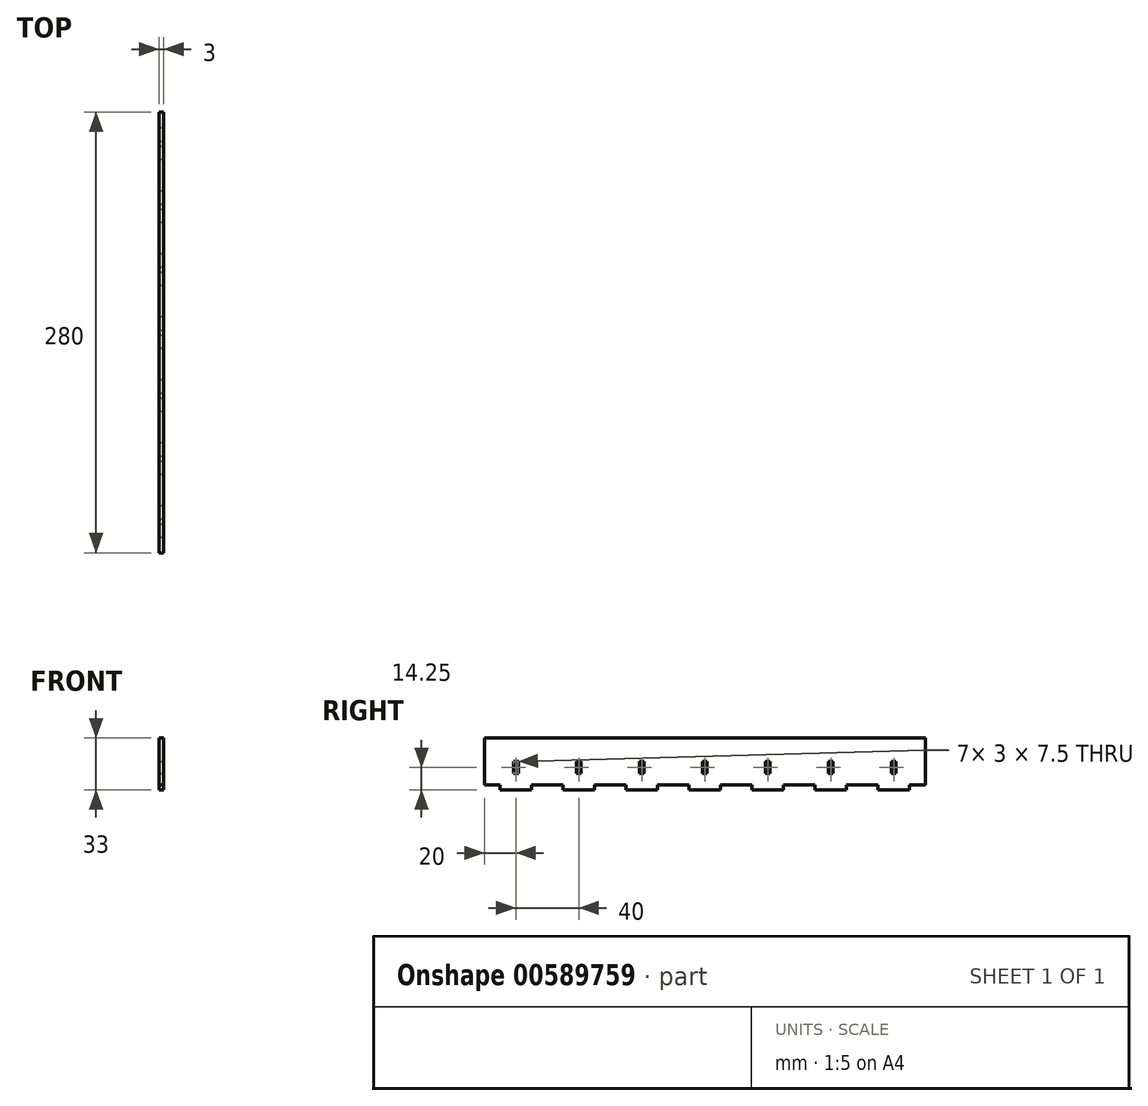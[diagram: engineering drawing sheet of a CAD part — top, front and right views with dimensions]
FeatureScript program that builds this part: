
annotation { "Feature Type Name" : "Feature", "Feature Type Description" : "" }
export const myFeature = defineFeature(function(context is Context, id is Id, definition is map)
    precondition{}
    {
        {
            var Q0;
            Q0=qCreatedBy(makeId("Right.planeOp"),FACE);
            var sketch = newSketch(context, id + "F0", { "sketchPlane" : qUnion([Q0])});
            skLineSegment(sketch, "E0.bottom", {"start": v(140, -15) * mm, "end": v(-140, -15) * mm});
            skLineSegment(sketch, "E0.top", {"start": v(140, 15) * mm, "end": v(-140, 15) * mm});
            skLineSegment(sketch, "E0.left", {"start": v(140, -15) * mm, "end": v(140, 15) * mm});
            skLineSegment(sketch, "E0.right", {"start": v(-140, -15) * mm, "end": v(-140, 15) * mm});
            skPoint(sketch, "E0.middle", {"position": v(0, 0) * mm});
            skSolve(sketch);
        }
        {
            var Q0;
            Q0 = qSketchRegion(id + "F0", true);
            extrude(context, id + "F1", {"entities" : qUnion([Q0]), "depth" : 3 * mm, "offsetDistance" : 25 * mm});
        }
        {
            var Q0;
            Q0=makeQuery(id+"F1.opExtrude","CAP_FACE",FACE,{"disambiguationData":[OSD([sQuery(id+"F0.wireOp",EDGE,"E0.bottom"),sQuery(id+"F0.wireOp",EDGE,"E0.top"),sQuery(id+"F0.wireOp",EDGE,"E0.left"),sQuery(id+"F0.wireOp",EDGE,"E0.right")])],"isStart":false});
            var sketch = newSketch(context, id + "F2", { "sketchPlane" : qUnion([Q0])});
            skLineSegment(sketch, "E1", {"start": v(140, -15) * mm, "end": v(130, -15) * mm, "construction": true});
            skLineSegment(sketch, "E2.bottom", {"start": v(130, -15) * mm, "end": v(110, -15) * mm});
            skLineSegment(sketch, "E2.top", {"start": v(130, -18) * mm, "end": v(110, -18) * mm});
            skLineSegment(sketch, "E2.left", {"start": v(130, -15) * mm, "end": v(130, -18) * mm});
            skLineSegment(sketch, "E2.right", {"start": v(110, -15) * mm, "end": v(110, -18) * mm});
            skLineSegment(sketch, "E3.1.0.0", {"start": v(90, -15) * mm, "end": v(90, -18) * mm});
            skLineSegment(sketch, "E3.1.0.1", {"start": v(90, -15) * mm, "end": v(70, -15) * mm});
            skLineSegment(sketch, "E3.1.0.2", {"start": v(90, -18) * mm, "end": v(70, -18) * mm});
            skLineSegment(sketch, "E3.1.0.3", {"start": v(70, -15) * mm, "end": v(70, -18) * mm});
            skLineSegment(sketch, "E3.2.0.0", {"start": v(50, -15) * mm, "end": v(50, -18) * mm});
            skLineSegment(sketch, "E3.2.0.1", {"start": v(50, -15) * mm, "end": v(30, -15) * mm});
            skLineSegment(sketch, "E3.2.0.2", {"start": v(50, -18) * mm, "end": v(30, -18) * mm});
            skLineSegment(sketch, "E3.2.0.3", {"start": v(30, -15) * mm, "end": v(30, -18) * mm});
            skLineSegment(sketch, "E3.3.0.0", {"start": v(10, -15) * mm, "end": v(10, -18) * mm});
            skLineSegment(sketch, "E3.3.0.1", {"start": v(10, -15) * mm, "end": v(-10, -15) * mm});
            skLineSegment(sketch, "E3.3.0.2", {"start": v(10, -18) * mm, "end": v(-10, -18) * mm});
            skLineSegment(sketch, "E3.3.0.3", {"start": v(-10, -15) * mm, "end": v(-10, -18) * mm});
            skLineSegment(sketch, "E3.4.0.0", {"start": v(-30, -15) * mm, "end": v(-30, -18) * mm});
            skLineSegment(sketch, "E3.4.0.1", {"start": v(-30, -15) * mm, "end": v(-50, -15) * mm});
            skLineSegment(sketch, "E3.4.0.2", {"start": v(-30, -18) * mm, "end": v(-50, -18) * mm});
            skLineSegment(sketch, "E3.4.0.3", {"start": v(-50, -15) * mm, "end": v(-50, -18) * mm});
            skLineSegment(sketch, "E3.5.0.0", {"start": v(-70, -15) * mm, "end": v(-70, -18) * mm});
            skLineSegment(sketch, "E3.5.0.1", {"start": v(-70, -15) * mm, "end": v(-90, -15) * mm});
            skLineSegment(sketch, "E3.5.0.2", {"start": v(-70, -18) * mm, "end": v(-90, -18) * mm});
            skLineSegment(sketch, "E3.5.0.3", {"start": v(-90, -15) * mm, "end": v(-90, -18) * mm});
            skLineSegment(sketch, "E3.6.0.0", {"start": v(-110, -15) * mm, "end": v(-110, -18) * mm});
            skLineSegment(sketch, "E3.6.0.1", {"start": v(-110, -15) * mm, "end": v(-130, -15) * mm});
            skLineSegment(sketch, "E3.6.0.2", {"start": v(-110, -18) * mm, "end": v(-130, -18) * mm});
            skLineSegment(sketch, "E3.6.0.3", {"start": v(-130, -15) * mm, "end": v(-130, -18) * mm});
            skLineSegment(sketch, "E3.direction1", {"start": v(130, -18) * mm, "end": v(90, -18) * mm, "construction": true});
            skSolve(sketch);
        }
        {
            var Q0;
            Q0 = qSketchRegion(id + "F2", true);
            var Q1;
            Q1=makeQuery(id+"F1.opExtrude","CAP_FACE",FACE,{"disambiguationData":[OSD([sQuery(id+"F0.wireOp",EDGE,"E0.bottom"),sQuery(id+"F0.wireOp",EDGE,"E0.top"),sQuery(id+"F0.wireOp",EDGE,"E0.left"),sQuery(id+"F0.wireOp",EDGE,"E0.right")])],"isStart":true});
            extrude(context, id + "F3", {"entities" : qUnion([Q0]), "operationType" : NewBodyOperationType.ADD, "endBound" : BoundingType.UP_TO_SURFACE, "oppositeDirection" : true, "depth" : 25 * mm, "endBoundEntityFace" : qUnion([Q1]), "offsetDistance" : 25 * mm});
        }
        {
            var Q0;
            Q0=makeQuery(id+"F3.boolean.opBoolean","MERGE",FACE,{"derivedFrom":[makeQuery(id+"F1.opExtrude","CAP_FACE",FACE,{"disambiguationData":[OSD([sQuery(id+"F0.wireOp",EDGE,"E0.bottom"),sQuery(id+"F0.wireOp",EDGE,"E0.top"),sQuery(id+"F0.wireOp",EDGE,"E0.left"),sQuery(id+"F0.wireOp",EDGE,"E0.right")])],"isStart":false}),makeQuery(id+"F3.opExtrude","CAP_FACE",FACE,{"disambiguationData":[OSD([sQuery(id+"F2.wireOp",EDGE,"E2.bottom"),sQuery(id+"F2.wireOp",EDGE,"E2.top"),sQuery(id+"F2.wireOp",EDGE,"E2.left"),sQuery(id+"F2.wireOp",EDGE,"E2.right")])],"isStart":true}),makeQuery(id+"F3.opExtrude","CAP_FACE",FACE,{"disambiguationData":[OSD([sQuery(id+"F2.wireOp",EDGE,"E3.1.0.0"),sQuery(id+"F2.wireOp",EDGE,"E3.1.0.1"),sQuery(id+"F2.wireOp",EDGE,"E3.1.0.2"),sQuery(id+"F2.wireOp",EDGE,"E3.1.0.3")])],"isStart":true}),makeQuery(id+"F3.opExtrude","CAP_FACE",FACE,{"disambiguationData":[OSD([sQuery(id+"F2.wireOp",EDGE,"E3.2.0.0"),sQuery(id+"F2.wireOp",EDGE,"E3.2.0.1"),sQuery(id+"F2.wireOp",EDGE,"E3.2.0.2"),sQuery(id+"F2.wireOp",EDGE,"E3.2.0.3")])],"isStart":true}),makeQuery(id+"F3.opExtrude","CAP_FACE",FACE,{"disambiguationData":[OSD([sQuery(id+"F2.wireOp",EDGE,"E3.3.0.0"),sQuery(id+"F2.wireOp",EDGE,"E3.3.0.1"),sQuery(id+"F2.wireOp",EDGE,"E3.3.0.2"),sQuery(id+"F2.wireOp",EDGE,"E3.3.0.3")])],"isStart":true}),makeQuery(id+"F3.opExtrude","CAP_FACE",FACE,{"disambiguationData":[OSD([sQuery(id+"F2.wireOp",EDGE,"E3.4.0.0"),sQuery(id+"F2.wireOp",EDGE,"E3.4.0.1"),sQuery(id+"F2.wireOp",EDGE,"E3.4.0.2"),sQuery(id+"F2.wireOp",EDGE,"E3.4.0.3")])],"isStart":true}),makeQuery(id+"F3.opExtrude","CAP_FACE",FACE,{"disambiguationData":[OSD([sQuery(id+"F2.wireOp",EDGE,"E3.5.0.0"),sQuery(id+"F2.wireOp",EDGE,"E3.5.0.1"),sQuery(id+"F2.wireOp",EDGE,"E3.5.0.2"),sQuery(id+"F2.wireOp",EDGE,"E3.5.0.3")])],"isStart":true}),makeQuery(id+"F3.opExtrude","CAP_FACE",FACE,{"disambiguationData":[OSD([sQuery(id+"F2.wireOp",EDGE,"E3.6.0.0"),sQuery(id+"F2.wireOp",EDGE,"E3.6.0.1"),sQuery(id+"F2.wireOp",EDGE,"E3.6.0.2"),sQuery(id+"F2.wireOp",EDGE,"E3.6.0.3")])],"isStart":true})]});
            var sketch = newSketch(context, id + "F4", { "sketchPlane" : qUnion([Q0])});
            skLineSegment(sketch, "E4", {"start": v(130, -15) * mm, "end": v(110, -15) * mm, "construction": true});
            skLineSegment(sketch, "E5", {"start": v(120, -15) * mm, "end": v(120, -3.75) * mm, "construction": true});
            skLineSegment(sketch, "E6.bottom", {"start": v(121.5, -7.5) * mm, "end": v(118.5, -7.5) * mm});
            skLineSegment(sketch, "E6.top", {"start": v(121.5, 0) * mm, "end": v(118.5, 0) * mm});
            skLineSegment(sketch, "E6.left", {"start": v(121.5, -7.5) * mm, "end": v(121.5, 0) * mm});
            skLineSegment(sketch, "E6.right", {"start": v(118.5, -7.5) * mm, "end": v(118.5, 0) * mm});
            skPoint(sketch, "E6.middle", {"position": v(120, -3.75) * mm});
            skLineSegment(sketch, "E7.1.0.0", {"start": v(81.5, -7.5) * mm, "end": v(81.5, 0) * mm});
            skLineSegment(sketch, "E7.1.0.1", {"start": v(81.5, 0) * mm, "end": v(78.5, 0) * mm});
            skLineSegment(sketch, "E7.1.0.2", {"start": v(78.5, -7.5) * mm, "end": v(78.5, 0) * mm});
            skLineSegment(sketch, "E7.1.0.3", {"start": v(81.5, -7.5) * mm, "end": v(78.5, -7.5) * mm});
            skLineSegment(sketch, "E7.2.0.0", {"start": v(41.5, -7.5) * mm, "end": v(41.5, 0) * mm});
            skLineSegment(sketch, "E7.2.0.1", {"start": v(41.5, 0) * mm, "end": v(38.5, 0) * mm});
            skLineSegment(sketch, "E7.2.0.2", {"start": v(38.5, -7.5) * mm, "end": v(38.5, 0) * mm});
            skLineSegment(sketch, "E7.2.0.3", {"start": v(41.5, -7.5) * mm, "end": v(38.5, -7.5) * mm});
            skLineSegment(sketch, "E7.3.0.0", {"start": v(1.5, -7.5) * mm, "end": v(1.5, 0) * mm});
            skLineSegment(sketch, "E7.3.0.1", {"start": v(1.5, 0) * mm, "end": v(-1.5, 0) * mm});
            skLineSegment(sketch, "E7.3.0.2", {"start": v(-1.5, -7.5) * mm, "end": v(-1.5, 0) * mm});
            skLineSegment(sketch, "E7.3.0.3", {"start": v(1.5, -7.5) * mm, "end": v(-1.5, -7.5) * mm});
            skLineSegment(sketch, "E7.4.0.0", {"start": v(-38.5, -7.5) * mm, "end": v(-38.5, 0) * mm});
            skLineSegment(sketch, "E7.4.0.1", {"start": v(-38.5, 0) * mm, "end": v(-41.5, 0) * mm});
            skLineSegment(sketch, "E7.4.0.2", {"start": v(-41.5, -7.5) * mm, "end": v(-41.5, 0) * mm});
            skLineSegment(sketch, "E7.4.0.3", {"start": v(-38.5, -7.5) * mm, "end": v(-41.5, -7.5) * mm});
            skLineSegment(sketch, "E7.5.0.0", {"start": v(-78.5, -7.5) * mm, "end": v(-78.5, 0) * mm});
            skLineSegment(sketch, "E7.5.0.1", {"start": v(-78.5, 0) * mm, "end": v(-81.5, 0) * mm});
            skLineSegment(sketch, "E7.5.0.2", {"start": v(-81.5, -7.5) * mm, "end": v(-81.5, 0) * mm});
            skLineSegment(sketch, "E7.5.0.3", {"start": v(-78.5, -7.5) * mm, "end": v(-81.5, -7.5) * mm});
            skLineSegment(sketch, "E7.6.0.0", {"start": v(-118.5, -7.5) * mm, "end": v(-118.5, 0) * mm});
            skLineSegment(sketch, "E7.6.0.1", {"start": v(-118.5, 0) * mm, "end": v(-121.5, 0) * mm});
            skLineSegment(sketch, "E7.6.0.2", {"start": v(-121.5, -7.5) * mm, "end": v(-121.5, 0) * mm});
            skLineSegment(sketch, "E7.6.0.3", {"start": v(-118.5, -7.5) * mm, "end": v(-121.5, -7.5) * mm});
            skLineSegment(sketch, "E7.direction1", {"start": v(121.5, -7.5) * mm, "end": v(81.5, -7.5) * mm, "construction": true});
            skSolve(sketch);
        }
        {
            var Q0;
            Q0 = qSketchRegion(id + "F4", true);
            extrude(context, id + "F5", {"entities" : qUnion([Q0]), "operationType" : NewBodyOperationType.REMOVE, "oppositeDirection" : true, "depth" : 25 * mm, "offsetDistance" : 25 * mm});
        }
    });
